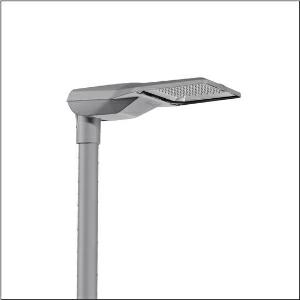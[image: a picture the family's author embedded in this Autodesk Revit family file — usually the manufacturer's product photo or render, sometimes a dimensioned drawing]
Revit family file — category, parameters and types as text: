
# Revit family: streetlight_sl_21_iq_midi___st0_5a_5xe3b41d08mb_eec4
name_source: partatom
category: Lighting Fixtures
units: mm (PartAtom-declared; Revit-internal decimal feet)

## family parameters
Cut with Voids When Loaded = No
Host = Face
Light Source = No
Part Type = Normal
Room Calculation Point = No
Round Connector Dimension = Use Diameter
Shared = No

## types (1)
- --- (1 x LED, 20360 lm, 146.7 W, 4000K)
    Apparent Load = 147 VA
    CIE Flux Codes = 41 75 97 100 100
    Color Rendering = 70
    Color Temperature = 4000K
    Default Elevation = 1800 mm
    Description = Streetlight SL 21 iQ midi, mast luminaire, primary light control with lens, of PMMA, primary optical cover: cover, of toughened safety glass, transparent, light distribution: ST0.5a, light emission: direct distribution, primary light characteristic: asymmetric, installation type: post-top, side-entry, LED, High Power LED, rated luminous flux: 20.360lm, luminous efficacy: 139lm/W, light colour: 740, colour temperature: 4000K, control: Auto-Match, Temp-Guard, Lumen-Switch, Night-Set, Smart-Wire, Light-Fading, Desk-Remote (wireless, voltage-free reading and setting of iQ features in the workshop via application-optimized NFC function/RFID function), optimised constant luminous flux control (CLO 2.0), presetting dimming linear, mains connection: 230..240V, AC, 50/60Hz, start of lifetime: 147W, end of service life: 161W, reduction: 62W, luminaire housing, of diecast aluminium, powder-coated, Siteco® metallic grey (DB 702S), corrosivity category C5 mid according to DIN EN ISO 12944, please order mast flange separately, inclination adjustable: 0°, 5°, 10°, 15°, sealing non-destructively replaceable, multi-level sealing system, length: 644mm, width: 335mm, height: 110mm, mast flange for spigot size: 42mm (side-entry): 5XC10008XM4, 60/48mm (side-entry/post-top): 5XC10108XM2, 76/60mm (side-entry/post-top): 5XC10108XM1, protection rating (complete): IP66, insulation class (complete): insulation class II (safety insulation), certification: CE, ENEC, ENEC+, VDE, impact resistance: IK09, permissible operating ambient temperature for outdoor applications: -40..+50°C, standard-compliant lighting for roads and squares, packaging unit: 1 piece

Light Distribution: ST0.5a
    Height = 111 mm
    Lamp = 1 x LED
    Lamp Light Flux = 20360 lm
    Lamp Power = 146.7 W
    Lamp count = 1
    Length = 644 mm
    Luminous efficacy = 139 lm/W
    Manufacturer = Siteco
    ModVariant = No
    Model = 5XE3B41D08MB
    Number of Poles = 1
    OnlyDefault = Yes
    Power Factor = 1
    Product Name = Streetlight SL 21 iQ midi | ST0.5a
    Product group = mast luminaire | pylon top
    ProductGroupID = 6100
    Protection Class = Protection class II
    Protection Degree = IP 66
    RLX_Detail_Level = 1
    RLX_Emergency_Light_Flux = 0 lm
    RLX_Emergency_Type = 0
    RLX_Emergency_Type_DB = No
    RlxData = <blob elided: 101673 chars, md5=c3c343e7>
    Socket = socket
    Standby Power = 0 W
    System Light Flux = 20360 lm
    System Power = 147 W
    Type Comments = factory setting: luminous flux: 100 % | dim-lin: 254 | 753 mA
    Type Image = l_1004298.jpg
    URL = http://relux.com
    VarID = @adj_126093
    Voltage = 0 V
    Weight = 0.00 kg
    Width = 336 mm

## geometry (parser evidence)
native form markers: Blend x4, Sweep x11
no freeform markers — native parametric forms only
